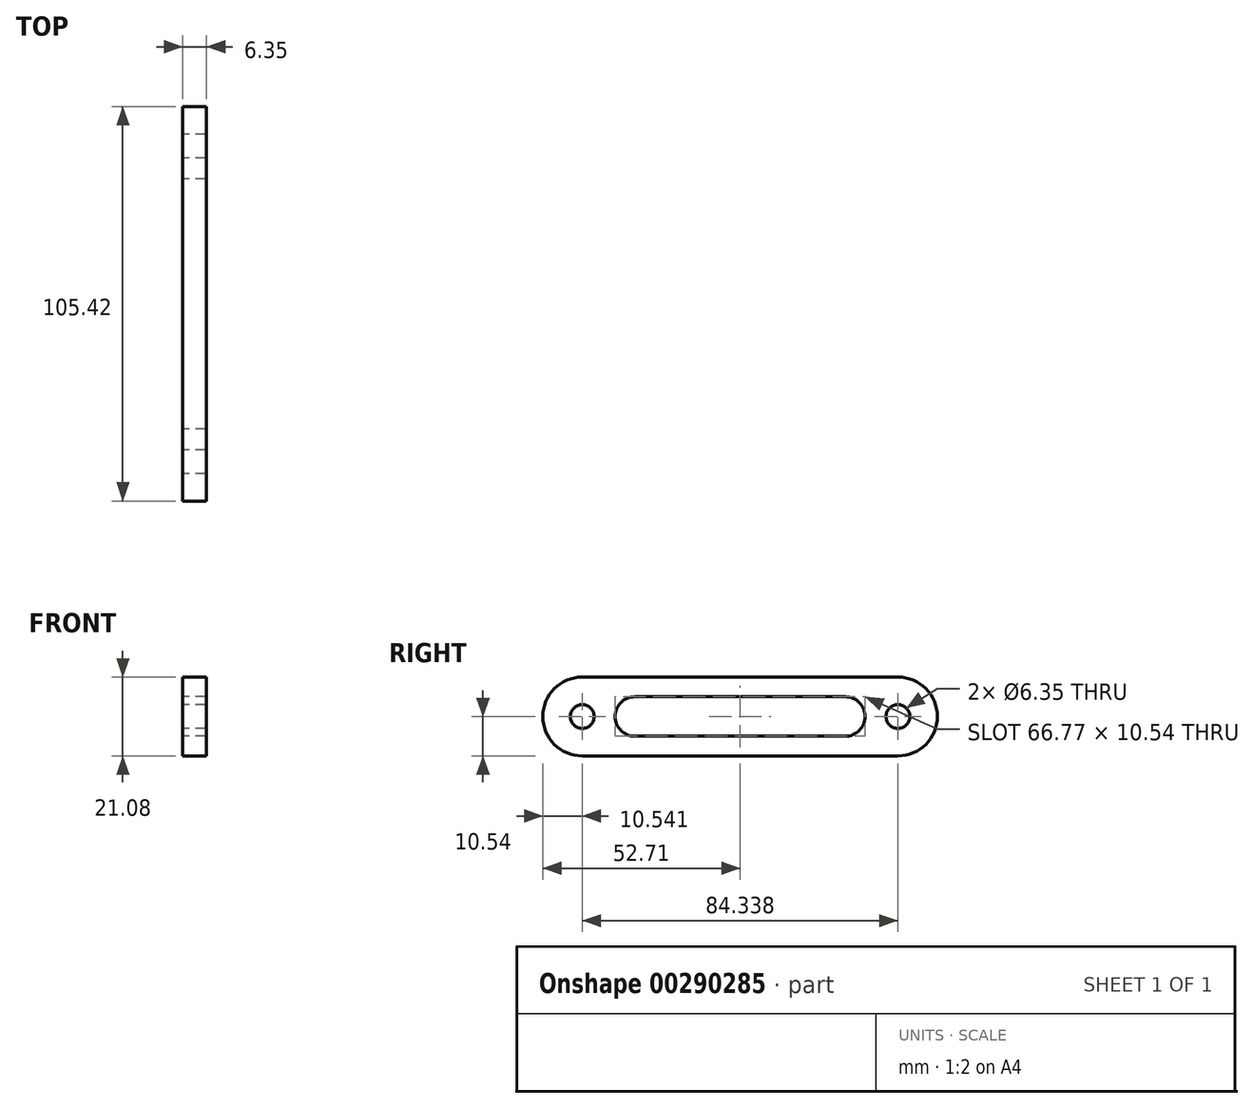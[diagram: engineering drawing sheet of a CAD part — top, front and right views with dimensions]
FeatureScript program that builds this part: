
annotation { "Feature Type Name" : "Feature", "Feature Type Description" : "" }
export const myFeature = defineFeature(function(context is Context, id is Id, definition is map)
    precondition{}
    {
        {
            var Q0;
            Q0=qCreatedBy(makeId("Right.planeOp"),FACE);
            var sketch = newSketch(context, id + "F0", { "sketchPlane" : qUnion([Q0])});
            skLineSegment(sketch, "E0.bottom", {"start": v(42.17, -10.54) * mm, "end": v(-42.17, -10.54) * mm});
            skLineSegment(sketch, "E0.top", {"start": v(42.17, 10.54) * mm, "end": v(-42.17, 10.54) * mm});
            skLineSegment(sketch, "E0.left", {"start": v(42.17, -10.54) * mm, "end": v(42.17, 10.54) * mm});
            skLineSegment(sketch, "E0.right", {"start": v(-42.17, -10.54) * mm, "end": v(-42.17, 10.54) * mm});
            skPoint(sketch, "E0.middle", {"position": v(0, 0) * mm});
            skArc(sketch, "E1", {"start": v(42.17, -10.54) * mm, "mid": v(52.71, 0) * mm, "end": v(42.17, 10.54) * mm});
            skArc(sketch, "E2", {"start": v(-42.17, 10.54) * mm, "mid": v(-52.71, 0) * mm, "end": v(-42.17, -10.54) * mm});
            skLineSegment(sketch, "E3.bottom", {"start": v(28.11, -5.27) * mm, "end": v(-28.11, -5.27) * mm});
            skLineSegment(sketch, "E3.top", {"start": v(28.11, 5.27) * mm, "end": v(-28.11, 5.27) * mm});
            skLineSegment(sketch, "E3.left", {"start": v(28.11, -5.27) * mm, "end": v(28.11, 5.27) * mm});
            skArc(sketch, "E4", {"start": v(-28.11, 5.27) * mm, "mid": v(-33.38, 0) * mm, "end": v(-28.11, -5.27) * mm});
            skArc(sketch, "E5", {"start": v(28.11, -5.27) * mm, "mid": v(33.38, 0) * mm, "end": v(28.11, 5.27) * mm});
            skCircle(sketch, "E6", {"center": v(42.17, 0) * mm, "radius": 3.18 * mm});
            skCircle(sketch, "E7", {"center": v(-42.17, 0) * mm, "radius": 3.18 * mm});
            skSolve(sketch);
        }
        {
            var Q0;
            Q0 = qSketchRegion(id + "F0", true);
            extrude(context, id + "F1", {"entities" : qUnion([Q0]), "depth" : 6.35 * mm});
        }
    });
